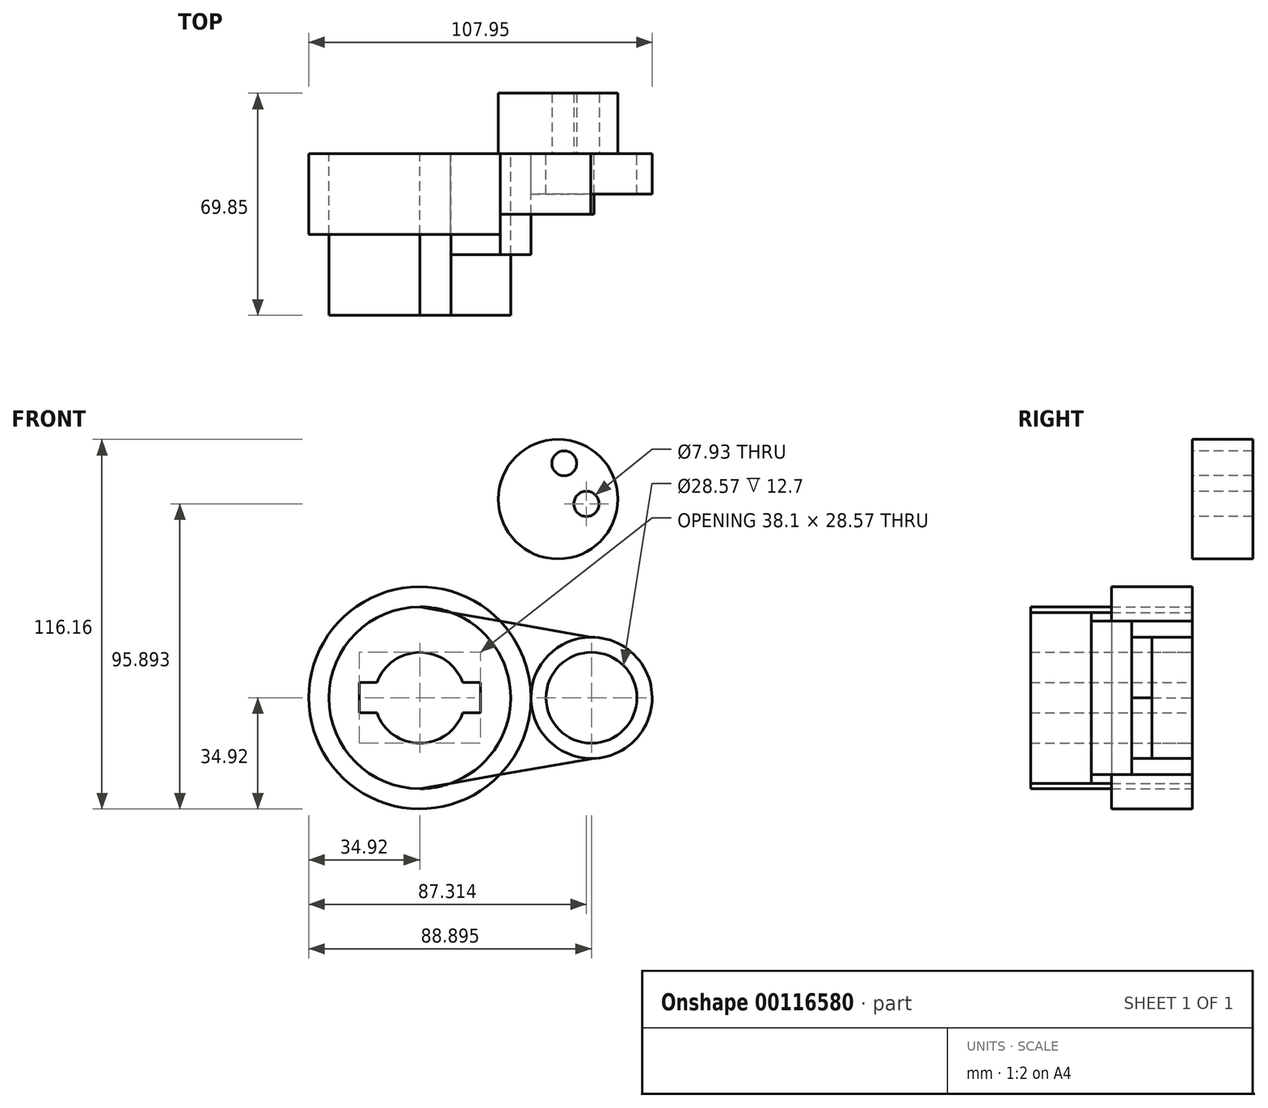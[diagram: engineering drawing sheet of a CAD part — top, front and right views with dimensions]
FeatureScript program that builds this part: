
annotation { "Feature Type Name" : "Feature", "Feature Type Description" : "" }
export const myFeature = defineFeature(function(context is Context, id is Id, definition is map)
    precondition{}
    {
        {
            var Q0;
            Q0=qCreatedBy(makeId("Front.planeOp"),FACE);
            var sketch = newSketch(context, id + "F0", { "sketchPlane" : qUnion([Q0])});
            skCircle(sketch, "E0", {"center": v(0, 0) * mm, "radius": 28.58 * mm});
            skCircle(sketch, "E1", {"center": v(53.97, 0) * mm, "radius": 19.05 * mm});
            skLineSegment(sketch, "E2", {"start": v(54.8, -19.03) * mm, "end": v(0, -28.57) * mm});
            skCircle(sketch, "E3", {"center": v(0, 0) * mm, "radius": 14.29 * mm});
            skCircle(sketch, "E4", {"center": v(53.97, 0) * mm, "radius": 14.29 * mm});
            skLineSegment(sketch, "E5", {"start": v(0, 28.58) * mm, "end": v(53.73, 19.05) * mm});
            skLineSegment(sketch, "E6.bottom", {"start": v(19.05, 4.76) * mm, "end": v(-19.05, 4.76) * mm});
            skLineSegment(sketch, "E6.top", {"start": v(19.05, -4.76) * mm, "end": v(-19.05, -4.76) * mm});
            skLineSegment(sketch, "E6.left", {"start": v(19.05, 4.76) * mm, "end": v(19.05, -4.76) * mm});
            skLineSegment(sketch, "E6.right", {"start": v(-19.05, 4.76) * mm, "end": v(-19.05, -4.76) * mm});
            skCircle(sketch, "E7.0", {"center": v(0, 0) * mm, "radius": 34.92 * mm});
            skCircle(sketch, "E8", {"center": v(43.46, 62.45) * mm, "radius": 18.8 * mm});
            skCircle(sketch, "E9", {"center": v(45.4, 73.7) * mm, "radius": 3.91 * mm});
            skCircle(sketch, "E10", {"center": v(52.4, 60.97) * mm, "radius": 3.96 * mm});
            skArc(sketch, "E11", {"start": v(32.62, 69.27) * mm, "mid": v(31.71, 55.73) * mm, "end": v(44.7, 51.74) * mm});
            skSolve(sketch);
        }
        {
            var Q0;
            {var subQ8=sQuery(id+"F0.wireOp",EDGE,"E6.left");Q0=makeQuery(id+"F0.imprint","IMPRINT",FACE,{"disambiguationData":[TD([[makeQuery(id+"F0.imprint","IMPRINT",EDGE,{"derivedFrom":subQ8}),1.0]])]});}
            extrude(context, id + "F1", {"entities" : qUnion([Q0]), "depth" : 50.8 * mm});
        }
        {
            var Q0;
            Q0=makeQuery(id+"F0.imprint","IMPRINT",FACE,{"disambiguationData":[TD([[makeQuery(id+"F0.imprint","IMPRINT",EDGE,{"derivedFrom":sQuery(id+"F0.wireOp",EDGE,"E4")}),-1.0]])]});
            extrude(context, id + "F2", {"entities" : qUnion([Q0]), "depth" : 12.7 * mm});
        }
        {
            var Q0;
            {var subQ0=sQuery(id+"F0.wireOp",EDGE,"E5");var subQ1=sQuery(id+"F0.wireOp",EDGE,"E0");var subQ2=makeQuery(id+"F0.imprint","INTERSECT",VERTEX,{"disambiguationData":[OD(1.0)],"derivedFrom":[subQ1,subQ0]});Q0=makeQuery(id+"F0.imprint","IMPRINT",FACE,{"disambiguationData":[TD([[makeQuery(id+"F0.imprint","IMPRINT",EDGE,{"disambiguationData":[TD([[subQ2,1.0]])],"derivedFrom":subQ1}),-1.0]])]});}
            extrude(context, id + "F3", {"entities" : qUnion([Q0]), "depth" : 25.4 * mm});
        }
        {
            var Q0;
            {var subQ3=sQuery(id+"F0.wireOp",EDGE,"E0");var subQ6=sQuery(id+"F0.wireOp",EDGE,"E5");var subQ7=makeQuery(id+"F0.imprint","INTERSECT",VERTEX,{"disambiguationData":[OD(0.0)],"derivedFrom":[subQ3,subQ6]});Q0=makeQuery(id+"F0.imprint","IMPRINT",FACE,{"disambiguationData":[TD([[makeQuery(id+"F0.imprint","IMPRINT",EDGE,{"disambiguationData":[TD([[subQ7,1.0]])],"derivedFrom":subQ3}),-1.0]])]});}
            extrude(context, id + "F4", {"entities" : qUnion([Q0]), "depth" : 31.75 * mm});
        }
        {
            var Q0;
            {var subQ0=sQuery(id+"F0.wireOp",EDGE,"E5");var subQ1=sQuery(id+"F0.wireOp",EDGE,"E1");var subQ2=makeQuery(id+"F0.imprint","INTERSECT",VERTEX,{"derivedFrom":[subQ1,subQ0]});Q0=makeQuery(id+"F0.imprint","IMPRINT",FACE,{"disambiguationData":[TD([[makeQuery(id+"F0.imprint","IMPRINT",EDGE,{"disambiguationData":[TD([[subQ2,-1.0]])],"derivedFrom":subQ1}),-1.0]])]});}
            extrude(context, id + "F5", {"entities" : qUnion([Q0]), "depth" : 19.05 * mm});
        }
        {
            var Q0;
            {var subQ0=sQuery(id+"F0.wireOp",EDGE,"E2");var subQ1=sQuery(id+"F0.wireOp",EDGE,"E1");var subQ2=makeQuery(id+"F0.imprint","INTERSECT",VERTEX,{"derivedFrom":[subQ1,subQ0]});Q0=makeQuery(id+"F0.imprint","IMPRINT",FACE,{"disambiguationData":[TD([[makeQuery(id+"F0.imprint","IMPRINT",EDGE,{"disambiguationData":[TD([[subQ2,1.0]])],"derivedFrom":subQ1}),-1.0]])]});}
            extrude(context, id + "F6", {"entities" : qUnion([Q0]), "depth" : 19.05 * mm});
        }
        {
            var Q0;
            Q0=makeQuery(id+"F0.imprint","IMPRINT",FACE,{"disambiguationData":[TD([[makeQuery(id+"F0.imprint","IMPRINT",EDGE,{"derivedFrom":sQuery(id+"F0.wireOp",EDGE,"E8")}),1.0]])]});
            extrude(context, id + "F7", {"entities" : qUnion([Q0]), "oppositeDirection" : true, "depth" : 19.05 * mm});
        }
    });
